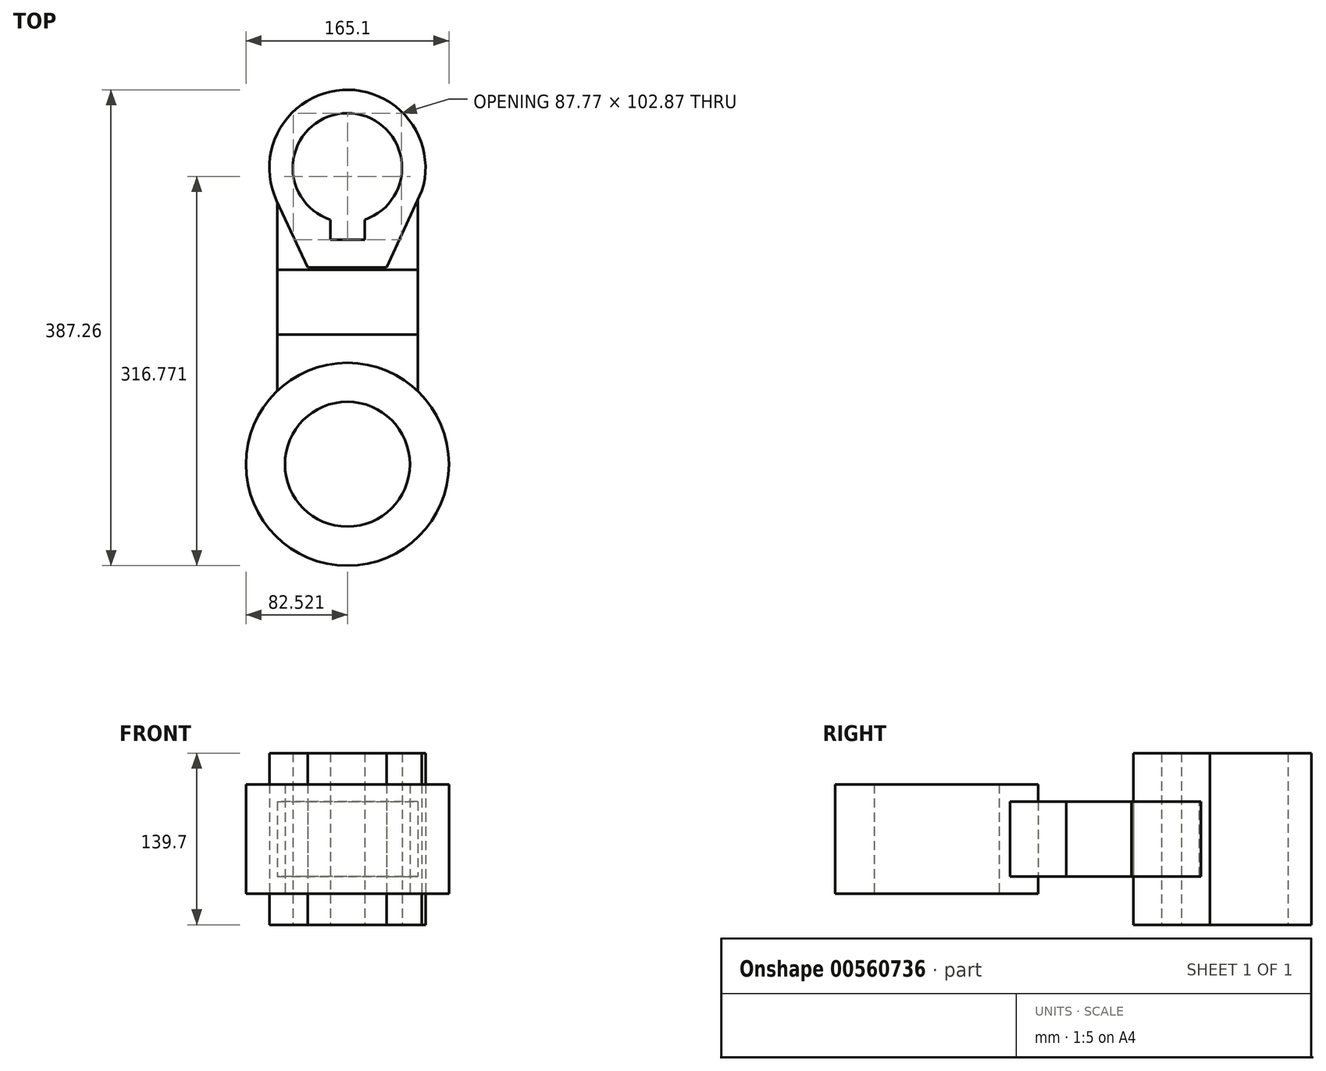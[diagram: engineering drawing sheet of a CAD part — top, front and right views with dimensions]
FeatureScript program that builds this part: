
annotation { "Feature Type Name" : "Feature", "Feature Type Description" : "" }
export const myFeature = defineFeature(function(context is Context, id is Id, definition is map)
    precondition{}
    {
        {
            var Q0;
            Q0=qCreatedBy(makeId("Top.planeOp"),FACE);
            var sketch = newSketch(context, id + "F0", { "sketchPlane" : qUnion([Q0])});
            skCircle(sketch, "E0", {"center": v(0, 0) * mm, "radius": 50.8 * mm});
            skCircle(sketch, "E1", {"center": v(0, 0) * mm, "radius": 82.55 * mm});
            skSolve(sketch);
        }
        {
            var Q0;
            Q0=makeQuery(id+"F0.imprint","IMPRINT",FACE,{"disambiguationData":[TD([[makeQuery(id+"F0.imprint","IMPRINT",EDGE,{"derivedFrom":sQuery(id+"F0.wireOp",EDGE,"E0")}),-1.0]])]});
            extrude(context, id + "F1", {"entities" : qUnion([Q0]), "depth" : 88.9 * mm, "offsetDistance" : 25.4 * mm});
        }
        {
            var Q0;
            Q0=qCreatedBy(makeId("Front.planeOp"),FACE);
            cPlane(context, id + "F2", {"entities" : qUnion([Q0]), "cplaneType" : CPlaneType.OFFSET, "offset" : 105.4 * mm, "oppositeDirection" : true, "width" : 152.4 * mm, "height" : 152.4 * mm});
        }
        {
            var Q0;
            Q0=qCreatedBy(id+"F2.planeOp",FACE);
            var sketch = newSketch(context, id + "F3", { "sketchPlane" : qUnion([Q0])});
            skLineSegment(sketch, "E2", {"start": v(-57.15, 13.97) * mm, "end": v(57.15, 13.97) * mm});
            skLineSegment(sketch, "E3", {"start": v(57.15, 13.97) * mm, "end": v(57.15, 74.93) * mm});
            skLineSegment(sketch, "E4", {"start": v(57.15, 74.93) * mm, "end": v(-57.15, 74.93) * mm});
            skLineSegment(sketch, "E5", {"start": v(-57.15, 74.93) * mm, "end": v(-57.15, 13.97) * mm});
            skSolve(sketch);
        }
        {
            var Q0;
            Q0 = qSketchRegion(id + "F3", true);
            extrude(context, id + "F4", {"entities" : qUnion([Q0]), "oppositeDirection" : true, "depth" : 52.83 * mm, "offsetDistance" : 25.4 * mm});
        }
        {
            var Q0;
            Q0=makeQuery(id+"F4.opExtrude","CAP_FACE",FACE,{"disambiguationData":[OSD([sQuery(id+"F3.wireOp",EDGE,"E2"),sQuery(id+"F3.wireOp",EDGE,"E3"),sQuery(id+"F3.wireOp",EDGE,"E4"),sQuery(id+"F3.wireOp",EDGE,"E5")])],"isStart":true});
            var Q1;
            Q1=makeQuery(id+"F1.opExtrude","SWEPT_BODY",BODY,{"disambiguationData":[OSD([sQuery(id+"F0.wireOp",EDGE,"E0"),sQuery(id+"F0.wireOp",EDGE,"E1")])]});
            extrude(context, id + "F5", {"entities" : qUnion([Q0]), "endBound" : BoundingType.UP_TO_BODY, "depth" : 25.4 * mm, "endBoundEntityBody" : qUnion([Q1]), "offsetDistance" : 25.4 * mm});
        }
        {
            var Q0;
            Q0=qCreatedBy(makeId("Top.planeOp"),FACE);
            var sketch = newSketch(context, id + "F6", { "sketchPlane" : qUnion([Q0])});
            skCircle(sketch, "E6", {"center": v(-0.03, 241.2) * mm, "radius": 44.45 * mm});
            skPoint(sketch, "E7.start.orphan", {"position": v(-0.03, 174.45) * mm});
            skPoint(sketch, "E8.end.orphan", {"position": v(69.82, 182.79) * mm});
            skPoint(sketch, "E9.end.orphan", {"position": v(44.42, 182.79) * mm});
            skLineSegment(sketch, "E10", {"start": v(-0.03, 182.79) * mm, "end": v(-14, 182.79) * mm});
            skLineSegment(sketch, "E11", {"start": v(-0.03, 182.79) * mm, "end": v(13.94, 182.79) * mm});
            skLineSegment(sketch, "E12", {"start": v(13.94, 182.79) * mm, "end": v(13.94, 199) * mm});
            skLineSegment(sketch, "E13", {"start": v(-14, 182.79) * mm, "end": v(-14, 199) * mm});
            skArc(sketch, "E14", {"start": v(53.18, 206.55) * mm, "mid": v(53.41, 206.9) * mm, "end": v(53.64, 207.26) * mm});
            skLineSegment(sketch, "E15", {"start": v(13.96, 159.99) * mm, "end": v(31.74, 159.99) * mm});
            skLineSegment(sketch, "E16", {"start": v(31.74, 159.99) * mm, "end": v(13.96, 159.99) * mm});
            skLineSegment(sketch, "E17", {"start": v(13.96, 159.99) * mm, "end": v(-32.39, 159.99) * mm});
            skLineSegment(sketch, "E18", {"start": v(31.74, 159.99) * mm, "end": v(60.56, 222.22) * mm});
            skLineSegment(sketch, "E19", {"start": v(-32.39, 159.99) * mm, "end": v(-57.65, 214.51) * mm});
            skPoint(sketch, "E20.orphan", {"position": v(-53.24, 206.55) * mm});
            skPoint(sketch, "E21.orphan", {"position": v(-61.21, 222.22) * mm});
            skArc(sketch, "E22.trimOffspring", {"start": v(60.56, 222.22) * mm, "mid": v(-4.16, 304.57) * mm, "end": v(-57.65, 214.51) * mm});
            skSolve(sketch);
        }
        {
            var Q0;
            Q0=makeQuery(id+"F6.imprint","IMPRINT",FACE,{"disambiguationData":[TD([[makeQuery(id+"F6.imprint","IMPRINT",EDGE,{"derivedFrom":sQuery(id+"F6.wireOp",EDGE,"E10")}),1.0]])]});
            extrude(context, id + "F7", {"entities" : qUnion([Q0]), "depth" : 44.45 * mm, "offsetDistance" : 25.4 * mm});
        }
        {
            var Q0;
            Q0=makeQuery(id+"F7.opExtrude","CAP_FACE",FACE,{"disambiguationData":[OSD([sQuery(id+"F6.wireOp",EDGE,"E6"),sQuery(id+"F6.wireOp",EDGE,"E10"),sQuery(id+"F6.wireOp",EDGE,"E11"),sQuery(id+"F6.wireOp",EDGE,"E12"),sQuery(id+"F6.wireOp",EDGE,"E13"),sQuery(id+"F6.wireOp",EDGE,"E16"),sQuery(id+"F6.wireOp",EDGE,"E17"),sQuery(id+"F6.wireOp",EDGE,"E18"),sQuery(id+"F6.wireOp",EDGE,"E19"),sQuery(id+"F6.wireOp",EDGE,"E22.trimOffspring")])],"isStart":true});
            extrude(context, id + "F8", {"entities" : qUnion([Q0]), "operationType" : NewBodyOperationType.ADD, "depth" : 25.4 * mm, "offsetDistance" : 25.4 * mm});
        }
        {
            var Q0;
            Q0=makeQuery(id+"F7.opExtrude","CAP_FACE",FACE,{"disambiguationData":[OSD([sQuery(id+"F6.wireOp",EDGE,"E6"),sQuery(id+"F6.wireOp",EDGE,"E10"),sQuery(id+"F6.wireOp",EDGE,"E11"),sQuery(id+"F6.wireOp",EDGE,"E12"),sQuery(id+"F6.wireOp",EDGE,"E13"),sQuery(id+"F6.wireOp",EDGE,"E16"),sQuery(id+"F6.wireOp",EDGE,"E17"),sQuery(id+"F6.wireOp",EDGE,"E18"),sQuery(id+"F6.wireOp",EDGE,"E19"),sQuery(id+"F6.wireOp",EDGE,"E22.trimOffspring")])],"isStart":false});
            extrude(context, id + "F9", {"entities" : qUnion([Q0]), "operationType" : NewBodyOperationType.ADD, "depth" : 69.85 * mm, "offsetDistance" : 25.4 * mm});
        }
        {
            var Q0;
            Q0=makeQuery(id+"F4.opExtrude","CAP_FACE",FACE,{"disambiguationData":[OSD([sQuery(id+"F3.wireOp",EDGE,"E2"),sQuery(id+"F3.wireOp",EDGE,"E3"),sQuery(id+"F3.wireOp",EDGE,"E4"),sQuery(id+"F3.wireOp",EDGE,"E5")])],"isStart":false});
            var Q1;
            Q1=makeQuery(id+"F7.opExtrude","SWEPT_BODY",BODY,{"disambiguationData":[OSD([sQuery(id+"F6.wireOp",EDGE,"E6"),sQuery(id+"F6.wireOp",EDGE,"E10"),sQuery(id+"F6.wireOp",EDGE,"E11"),sQuery(id+"F6.wireOp",EDGE,"E12"),sQuery(id+"F6.wireOp",EDGE,"E13"),sQuery(id+"F6.wireOp",EDGE,"E16"),sQuery(id+"F6.wireOp",EDGE,"E17"),sQuery(id+"F6.wireOp",EDGE,"E18"),sQuery(id+"F6.wireOp",EDGE,"E19"),sQuery(id+"F6.wireOp",EDGE,"E22.trimOffspring")])]});
            extrude(context, id + "F10", {"entities" : qUnion([Q0]), "endBound" : BoundingType.UP_TO_BODY, "depth" : 25.4 * mm, "endBoundEntityBody" : qUnion([Q1]), "offsetDistance" : 25.4 * mm});
        }
    });
